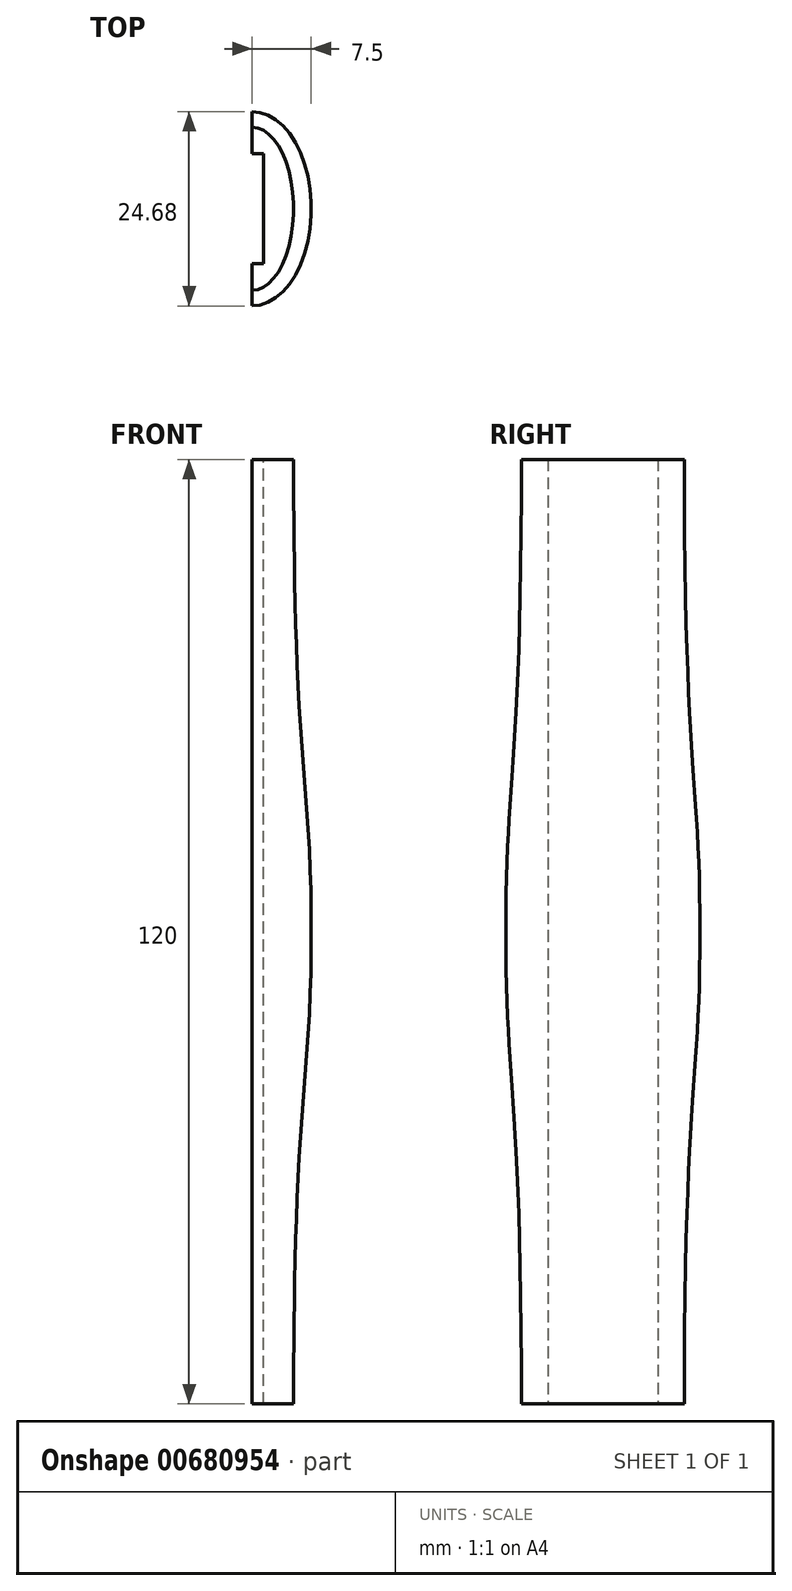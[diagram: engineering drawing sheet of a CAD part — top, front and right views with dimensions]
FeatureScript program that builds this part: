
annotation { "Feature Type Name" : "Feature", "Feature Type Description" : "" }
export const myFeature = defineFeature(function(context is Context, id is Id, definition is map)
    precondition{}
    {
        {
            var Q0;
            Q0=qCreatedBy(makeId("Top.planeOp"),FACE);
            var sketch = newSketch(context, id + "F0", { "sketchPlane" : qUnion([Q0])});
            skEllipticalArc(sketch, "E0", {});
            skLineSegment(sketch, "E1", {"start": v(0, -12.34) * mm, "end": v(0, 12.34) * mm});
            const initialGuessF0  = {"E0": [0, 0, 0, -1, 0.012335, 0.0075, 3.141592653589793, 0]};
            skSetInitialGuess(sketch, initialGuessF0);
            skSolve(sketch);
        }
        {
            var Q0;
            Q0=qCreatedBy(makeId("Top.planeOp"),FACE);
            cPlane(context, id + "F1", {"entities" : qUnion([Q0]), "cplaneType" : CPlaneType.OFFSET, "offset" : 60 * mm, "width" : 150 * mm, "height" : 150 * mm});
        }
        {
            var Q0;
            Q0=qCreatedBy(id+"F1.planeOp",FACE);
            var sketch = newSketch(context, id + "F2", { "sketchPlane" : qUnion([Q0])});
            skEllipticalArc(sketch, "E2", {});
            skLineSegment(sketch, "E3", {"start": v(0, 10.35) * mm, "end": v(0, -10.35) * mm});
            const initialGuessF2  = {"E2": [0, 0, 0, -1, 0.01035, 0.00525, 3.141592653589793, 0]};
            skSetInitialGuess(sketch, initialGuessF2);
            skSolve(sketch);
        }
        {
            var Q0;
            Q0=makeQuery(id+"F0.imprint","IMPRINT",FACE,{"disambiguationData":[TD([[makeQuery(id+"F0.imprint","IMPRINT",EDGE,{"derivedFrom":sQuery(id+"F0.wireOp",EDGE,"E0")}),1.0]])]});
            var Q1;
            Q1=makeQuery(id+"F2.imprint","IMPRINT",FACE,{"disambiguationData":[TD([[makeQuery(id+"F2.imprint","IMPRINT",EDGE,{"derivedFrom":sQuery(id+"F2.wireOp",EDGE,"E2")}),1.0]])]});
            loft(context, id + "F3", {"startCondition" : LoftEndDerivativeType.NORMAL_TO_PROFILE, "startMagnitude" : 1, "endCondition" : LoftEndDerivativeType.NORMAL_TO_PROFILE, "endMagnitude" : 2, "sheetProfilesArray" : [{ "sheetProfileEntities" : qUnion([Q0]) }, { "sheetProfileEntities" : qUnion([Q1]) }]});
        }
        {
            var Q0;
            Q0=makeQuery(id+"F3.opLoft","SWEPT_BODY",BODY,{"disambiguationData":[OSD([makeQuery(id+"F0.imprint","IMPRINT",FACE,{"disambiguationData":[TD([[makeQuery(id+"F0.imprint","IMPRINT",EDGE,{"derivedFrom":sQuery(id+"F0.wireOp",EDGE,"E0")}),1.0]])]}),makeQuery(id+"F2.imprint","IMPRINT",FACE,{"disambiguationData":[TD([[makeQuery(id+"F2.imprint","IMPRINT",EDGE,{"derivedFrom":sQuery(id+"F2.wireOp",EDGE,"E2")}),1.0]])]})])]});
            var Q1;
            Q1=qCreatedBy(makeId("Top.planeOp"),FACE);
            mirror(context, id + "F4", {"operationType" : NewBodyOperationType.ADD, "entities" : qUnion([Q0]), "mirrorPlane" : qUnion([Q1])});
        }
        {
            var Q0;
            Q0=makeQuery(id+"F3.opLoft","CAP_FACE",FACE,{"disambiguationData":[OSD([makeQuery(id+"F2.imprint","IMPRINT",FACE,{"disambiguationData":[TD([[makeQuery(id+"F2.imprint","IMPRINT",EDGE,{"derivedFrom":sQuery(id+"F2.wireOp",EDGE,"E2")}),1.0]])]})])],"isStart":true});
            var sketch = newSketch(context, id + "F5", { "sketchPlane" : qUnion([Q0])});
            skLineSegment(sketch, "E4.bottom", {"start": v(-1.43, 7) * mm, "end": v(1.44, 7) * mm});
            skLineSegment(sketch, "E4.top", {"start": v(-1.44, -7) * mm, "end": v(1.43, -7) * mm});
            skLineSegment(sketch, "E4.left", {"start": v(-1.43, 7) * mm, "end": v(-1.44, -7) * mm});
            skLineSegment(sketch, "E4.right", {"start": v(1.44, 7) * mm, "end": v(1.43, -7) * mm});
            skPoint(sketch, "E4.middle", {"position": v(0, 0) * mm});
            skSolve(sketch);
        }
        {
            var Q0;
            Q0=qSketchRegion(id+"F5",true);
            extrude(context, id + "F6", {"entities" : qUnion([Q0]), "operationType" : NewBodyOperationType.REMOVE, "oppositeDirection" : true, "depth" : 120 * mm, "offsetDistance" : 25 * mm});
        }
        {
            var Q0;
            Q0=makeQuery(id+"F3.opLoft","SWEPT_BODY",BODY,{"disambiguationData":[OSD([makeQuery(id+"F0.imprint","IMPRINT",FACE,{"disambiguationData":[TD([[makeQuery(id+"F0.imprint","IMPRINT",EDGE,{"derivedFrom":sQuery(id+"F0.wireOp",EDGE,"E0")}),1.0]])]}),makeQuery(id+"F2.imprint","IMPRINT",FACE,{"disambiguationData":[TD([[makeQuery(id+"F2.imprint","IMPRINT",EDGE,{"derivedFrom":sQuery(id+"F2.wireOp",EDGE,"E2")}),1.0]])]})])]});
            var Q1;
            Q1=qCreatedBy(makeId("Right.planeOp"),FACE);
            mirror(context, id + "F7", {"entities" : qUnion([Q0]), "mirrorPlane" : qUnion([Q1])});
        }
        {
            var Q0;
            Q0=makeQuery(id+"F3.opLoft","SWEPT_BODY",BODY,{"disambiguationData":[OSD([makeQuery(id+"F0.imprint","IMPRINT",FACE,{"disambiguationData":[TD([[makeQuery(id+"F0.imprint","IMPRINT",EDGE,{"derivedFrom":sQuery(id+"F0.wireOp",EDGE,"E0")}),1.0]])]}),makeQuery(id+"F2.imprint","IMPRINT",FACE,{"disambiguationData":[TD([[makeQuery(id+"F2.imprint","IMPRINT",EDGE,{"derivedFrom":sQuery(id+"F2.wireOp",EDGE,"E2")}),1.0]])]})])]});
            deleteBodies(context, id + "F8", {"entities" : qUnion([Q0])});
        }
    });
